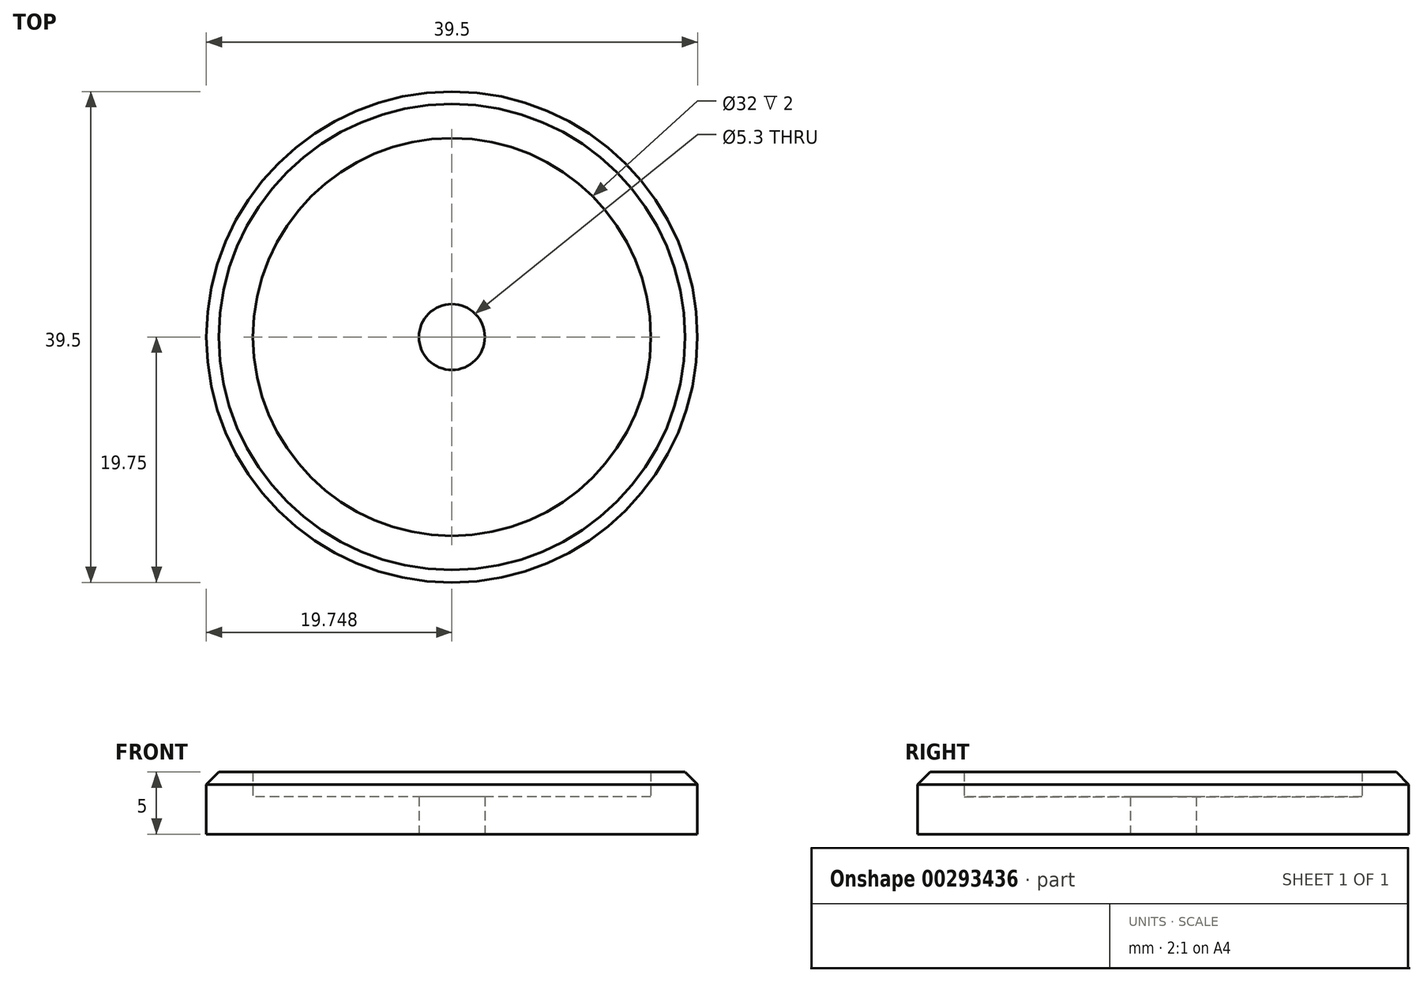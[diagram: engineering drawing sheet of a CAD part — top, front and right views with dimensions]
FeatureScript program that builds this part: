
annotation { "Feature Type Name" : "Feature", "Feature Type Description" : "" }
export const myFeature = defineFeature(function(context is Context, id is Id, definition is map)
    precondition{}
    {
        {
            var Q0;
            Q0=qCreatedBy(makeId("Top.planeOp"),FACE);
            var sketch = newSketch(context, id + "F0", { "sketchPlane" : qUnion([Q0])});
            skCircle(sketch, "E0", {"center": v(2.68, 0) * mm, "radius": 16 * mm});
            skCircle(sketch, "E1", {"center": v(2.68, 0) * mm, "radius": 19.75 * mm});
            skCircle(sketch, "E2", {"center": v(2.68, 0) * mm, "radius": 2.65 * mm});
            skSolve(sketch);
        }
        {
            var Q0;
            Q0=makeQuery(id+"F0.imprint","IMPRINT",FACE,{"disambiguationData":[TD([[makeQuery(id+"F0.imprint","IMPRINT",EDGE,{"derivedFrom":sQuery(id+"F0.wireOp",EDGE,"E0")}),-1.0]])]});
            extrude(context, id + "F1", {"entities" : qUnion([Q0]), "depth" : 5 * mm, "offsetDistance" : 25 * mm});
        }
        {
            var Q0;
            Q0=makeQuery(id+"F0.imprint","IMPRINT",FACE,{"disambiguationData":[TD([[makeQuery(id+"F0.imprint","IMPRINT",EDGE,{"derivedFrom":sQuery(id+"F0.wireOp",EDGE,"E0")}),1.0]])]});
            extrude(context, id + "F2", {"entities" : qUnion([Q0]), "operationType" : NewBodyOperationType.ADD, "depth" : 3 * mm, "offsetDistance" : 25 * mm});
        }
        {
            var Q0;
            Q0=makeQuery(id+"F1.opExtrude","CAP_EDGE",EDGE,{"disambiguationData":[OSD([sQuery(id+"F0.wireOp",EDGE,"E1")])],"isStart":false});
            chamfer(context, id + "F3", {"entities" : qUnion([Q0]), "width" : 1 * mm, "tangentPropagation" : true});
        }
    });
